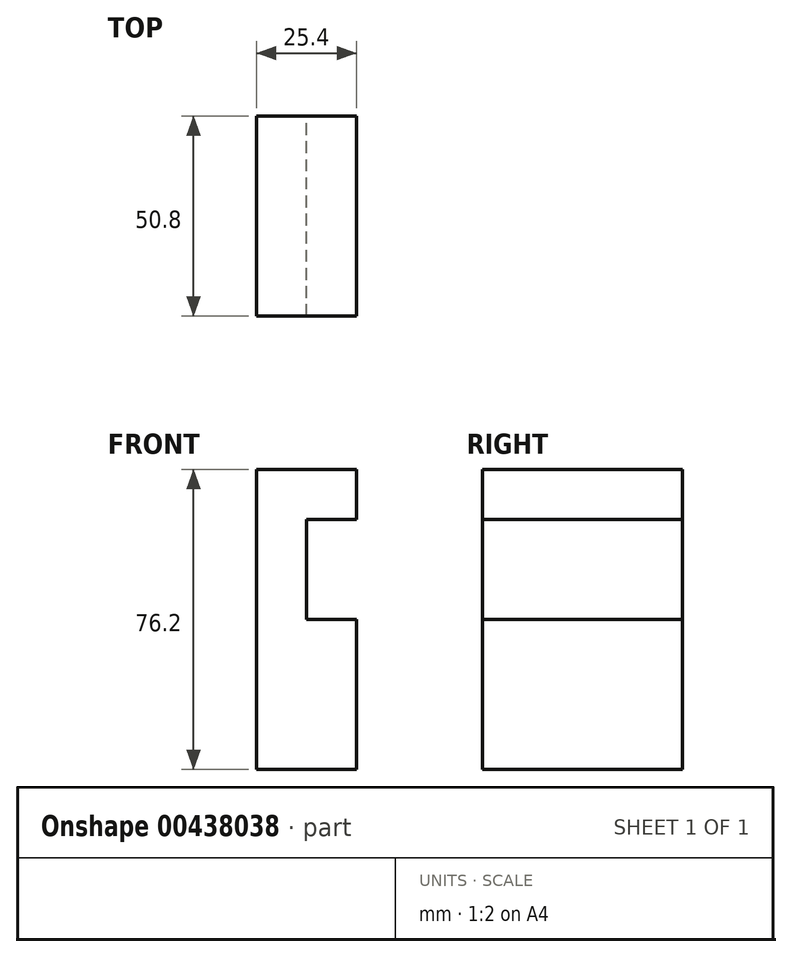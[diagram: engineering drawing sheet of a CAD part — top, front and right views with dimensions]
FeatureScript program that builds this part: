
annotation { "Feature Type Name" : "Feature", "Feature Type Description" : "" }
export const myFeature = defineFeature(function(context is Context, id is Id, definition is map)
    precondition{}
    {
        {
            var Q0;
            Q0=qCreatedBy(makeId("Front.planeOp"),FACE);
            var sketch = newSketch(context, id + "F0", { "sketchPlane" : qUnion([Q0])});
            skLineSegment(sketch, "E0", {"start": v(0, -24.78) * mm, "end": v(0, 51.42) * mm});
            skLineSegment(sketch, "E1", {"start": v(0, 51.42) * mm, "end": v(25.4, 51.42) * mm});
            skLineSegment(sketch, "E2", {"start": v(25.4, 51.42) * mm, "end": v(25.4, 38.72) * mm});
            skLineSegment(sketch, "E3", {"start": v(25.4, 38.72) * mm, "end": v(12.7, 38.72) * mm});
            skLineSegment(sketch, "E4", {"start": v(12.7, 38.72) * mm, "end": v(12.7, 13.32) * mm});
            skLineSegment(sketch, "E5", {"start": v(12.7, 13.32) * mm, "end": v(25.4, 13.32) * mm});
            skLineSegment(sketch, "E6", {"start": v(25.4, 13.32) * mm, "end": v(25.4, -24.78) * mm});
            skLineSegment(sketch, "E7", {"start": v(25.4, -24.78) * mm, "end": v(0, -24.78) * mm});
            skSolve(sketch);
        }
        {
            var Q0;
            Q0 = qSketchRegion(id + "F0", true);
            extrude(context, id + "F1", {"entities" : qUnion([Q0]), "depth" : 50.8 * mm});
        }
    });
